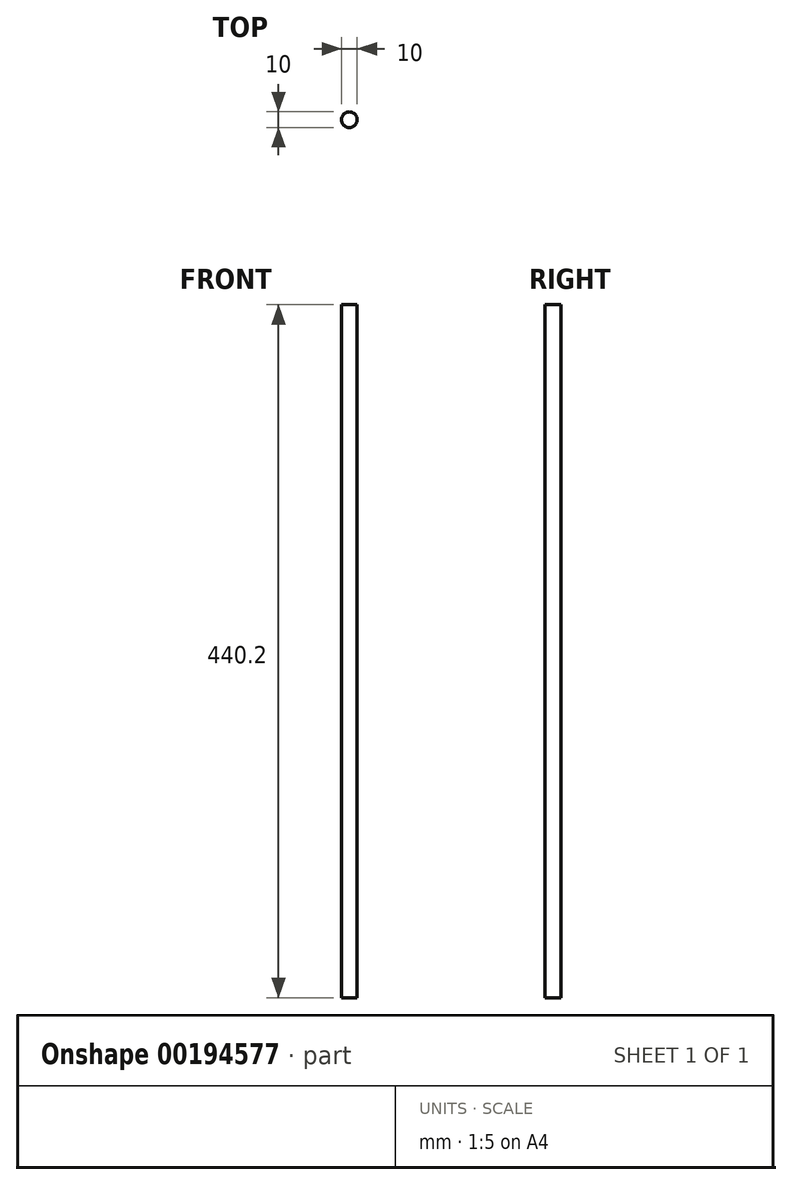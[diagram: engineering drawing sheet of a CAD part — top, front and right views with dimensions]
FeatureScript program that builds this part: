
annotation { "Feature Type Name" : "Feature", "Feature Type Description" : "" }
export const myFeature = defineFeature(function(context is Context, id is Id, definition is map)
    precondition{}
    {
        {
            var Q0;
            Q0=qCreatedBy(makeId("Top.planeOp"),FACE);
            var sketch = newSketch(context, id + "F0", { "sketchPlane" : qUnion([Q0])});
            skCircle(sketch, "E0", {"center": v(0, 0) * mm, "radius": 5 * mm});
            skSolve(sketch);
        }
        {
            var Q0;
            Q0 = qSketchRegion(id + "F0", true);
            extrude(context, id + "F1", {"entities" : qUnion([Q0]), "depth" : 440.2 * mm});
        }
    });
